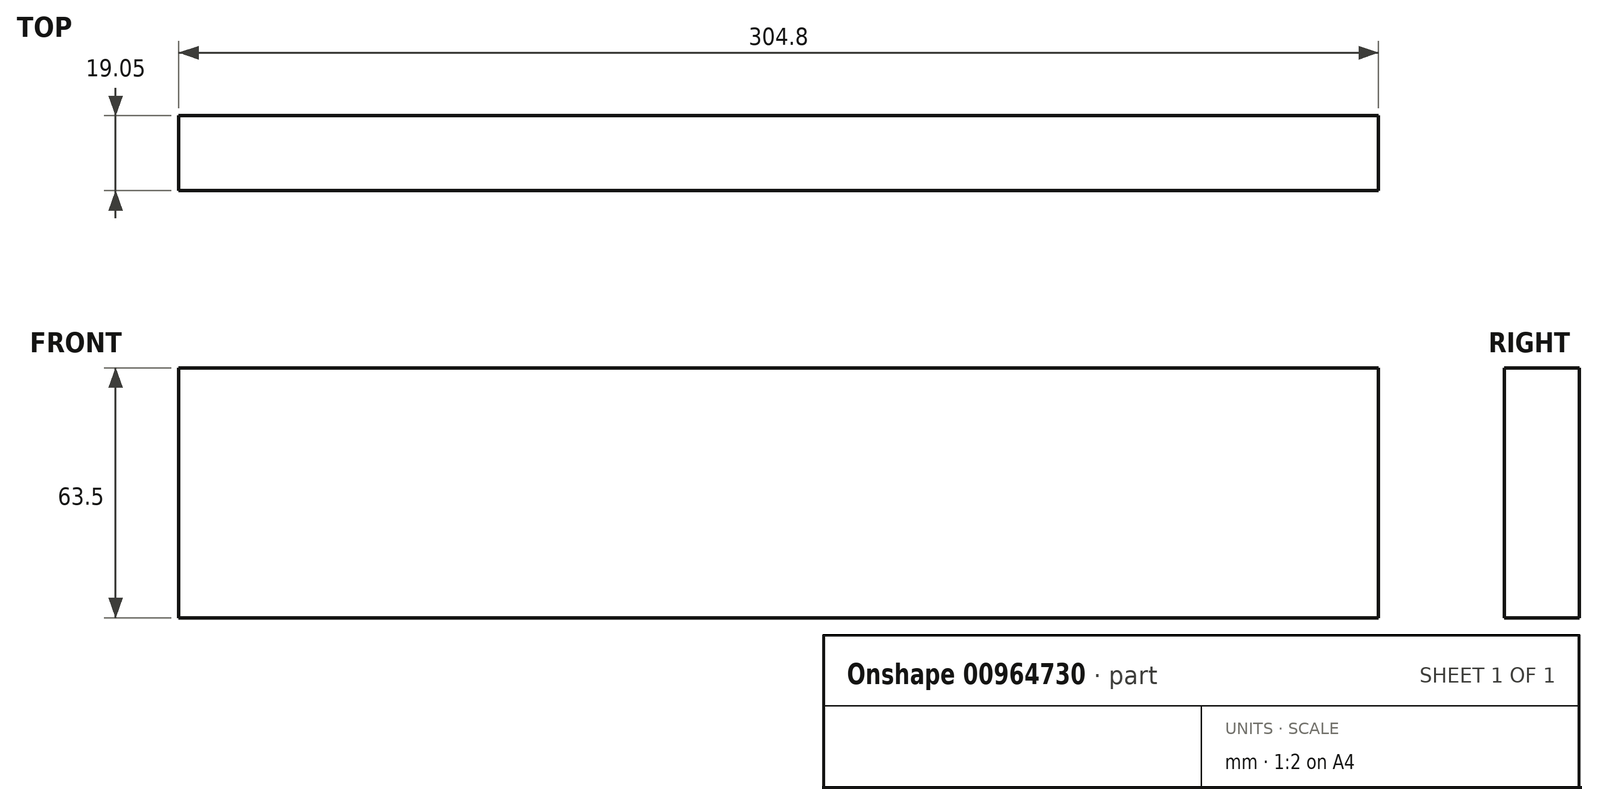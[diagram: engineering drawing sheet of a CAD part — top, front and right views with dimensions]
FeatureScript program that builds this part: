
annotation { "Feature Type Name" : "Feature", "Feature Type Description" : "" }
export const myFeature = defineFeature(function(context is Context, id is Id, definition is map)
    precondition{}
    {
        {
            var Q0;
            Q0=qCreatedBy(makeId("Front.planeOp"),FACE);
            var sketch = newSketch(context, id + "F0", { "sketchPlane" : qUnion([Q0])});
            skLineSegment(sketch, "E0.bottom", {"start": v(0, 0) * mm, "end": v(-304.8, 0) * mm});
            skLineSegment(sketch, "E0.top", {"start": v(0, 63.5) * mm, "end": v(-304.8, 63.5) * mm});
            skLineSegment(sketch, "E0.left", {"start": v(0, 0) * mm, "end": v(0, 63.5) * mm});
            skLineSegment(sketch, "E0.right", {"start": v(-304.8, 0) * mm, "end": v(-304.8, 63.5) * mm});
            skSolve(sketch);
        }
        {
            var Q0;
            Q0 = qSketchRegion(id + "F0", true);
            extrude(context, id + "F1", {"entities" : qUnion([Q0]), "depth" : 19.05 * mm, "offsetDistance" : 25.4 * mm});
        }
    });
